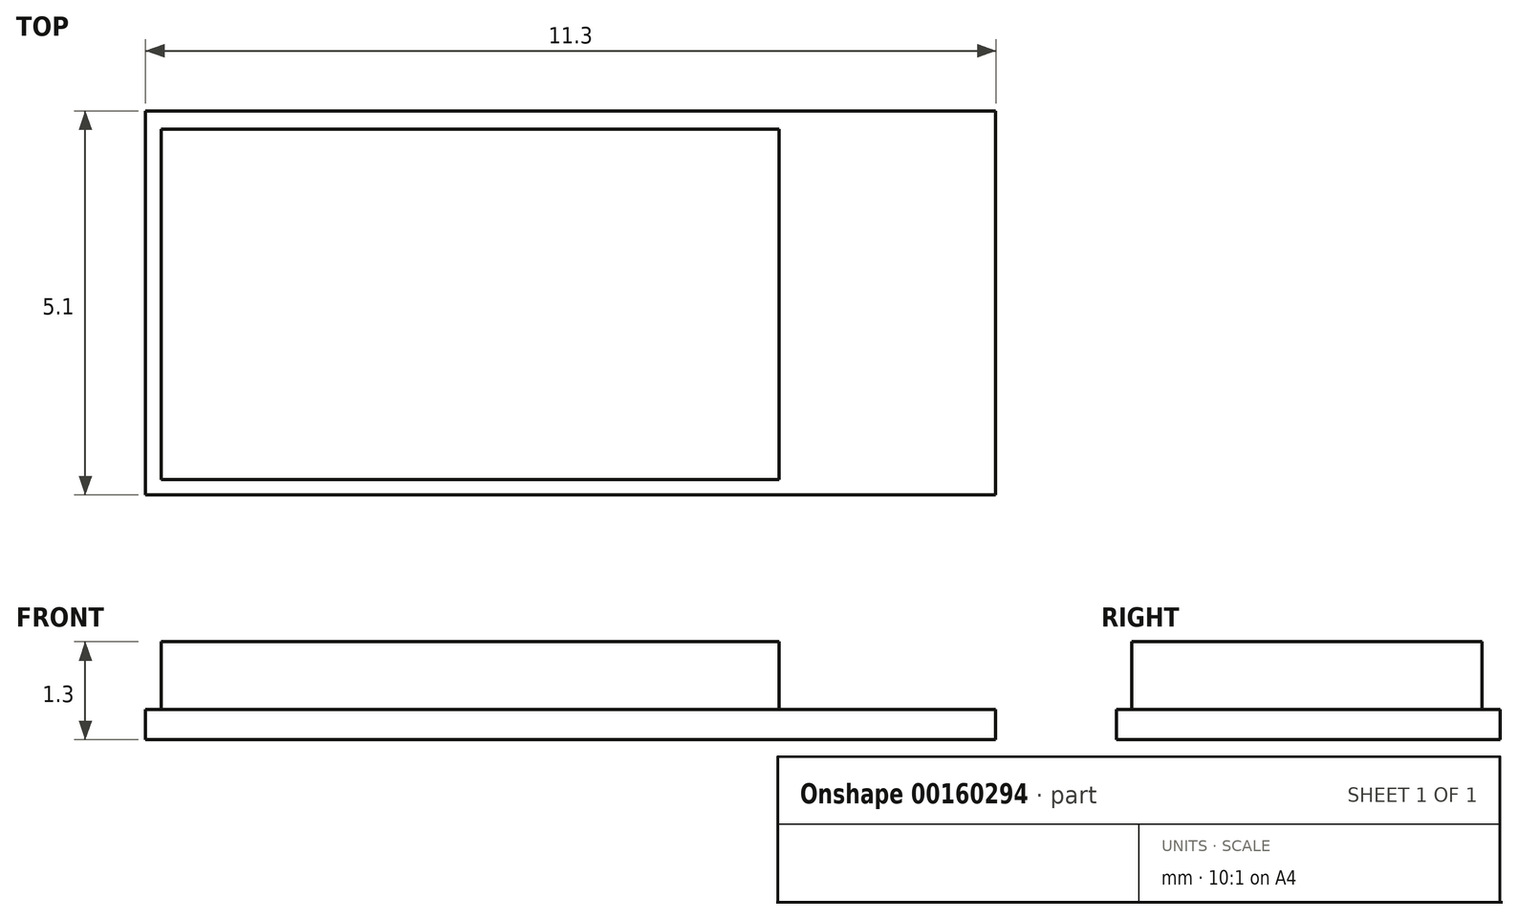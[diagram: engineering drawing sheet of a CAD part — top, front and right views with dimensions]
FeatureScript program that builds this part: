
annotation { "Feature Type Name" : "Feature", "Feature Type Description" : "" }
export const myFeature = defineFeature(function(context is Context, id is Id, definition is map)
    precondition{}
    {
        {
            var Q0;
            Q0=qCreatedBy(makeId("Top.planeOp"),FACE);
            var sketch = newSketch(context, id + "F0", { "sketchPlane" : qUnion([Q0])});
            skLineSegment(sketch, "E0.bottom", {"start": v(-5.4, 2.55) * mm, "end": v(5.9, 2.55) * mm});
            skLineSegment(sketch, "E0.top", {"start": v(-5.4, -2.55) * mm, "end": v(5.9, -2.55) * mm});
            skLineSegment(sketch, "E0.left", {"start": v(-5.4, 2.55) * mm, "end": v(-5.4, -2.55) * mm});
            skLineSegment(sketch, "E0.right", {"start": v(5.9, 2.55) * mm, "end": v(5.9, -2.55) * mm});
            skPoint(sketch, "E1", {"position": v(-5.4, 0) * mm});
            skSolve(sketch);
        }
        {
            var Q0;
            Q0 = qSketchRegion(id + "F0", true);
            extrude(context, id + "F1", {"entities" : qUnion([Q0]), "depth" : 0.4 * mm});
        }
        {
            var Q0;
            Q0=makeQuery(id+"F1.opExtrude","CAP_FACE",FACE,{"disambiguationData":[OSD([sQuery(id+"F0.wireOp",EDGE,"E0.bottom"),sQuery(id+"F0.wireOp",EDGE,"E0.top"),sQuery(id+"F0.wireOp",EDGE,"E0.left"),sQuery(id+"F0.wireOp",EDGE,"E0.right")])],"isStart":false});
            var sketch = newSketch(context, id + "F2", { "sketchPlane" : qUnion([Q0])});
            skLineSegment(sketch, "E2.bottom", {"start": v(-5.18, 2.3) * mm, "end": v(3.03, 2.3) * mm});
            skLineSegment(sketch, "E2.top", {"start": v(-5.18, -2.35) * mm, "end": v(3.03, -2.35) * mm});
            skLineSegment(sketch, "E2.left", {"start": v(-5.18, 2.3) * mm, "end": v(-5.18, -2.35) * mm});
            skLineSegment(sketch, "E2.right", {"start": v(3.03, 2.3) * mm, "end": v(3.03, -2.35) * mm});
            skSolve(sketch);
        }
        {
            var Q0;
            Q0 = qSketchRegion(id + "F2", true);
            extrude(context, id + "F3", {"entities" : qUnion([Q0]), "operationType" : NewBodyOperationType.ADD, "depth" : (1.3 - 0.4) * mm});
        }
    });
